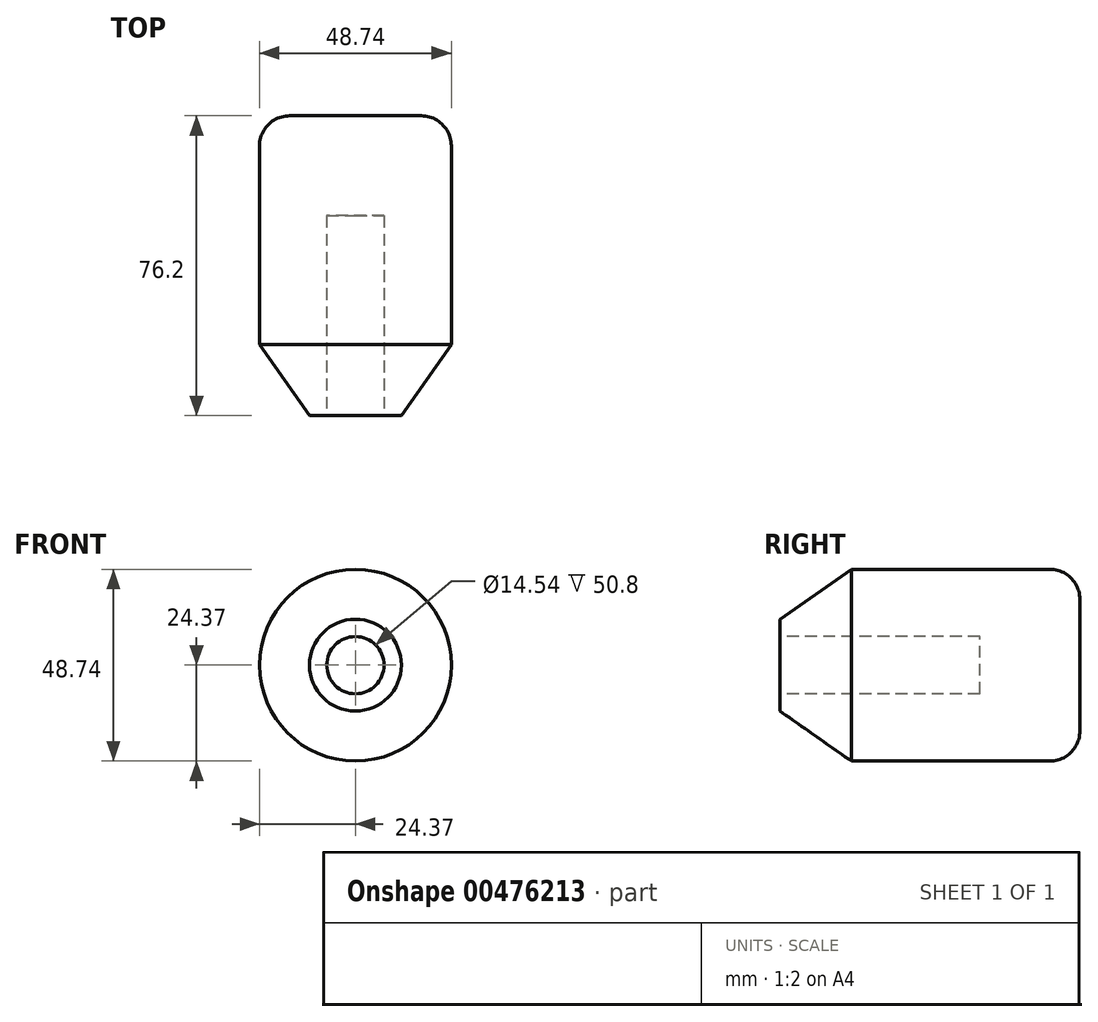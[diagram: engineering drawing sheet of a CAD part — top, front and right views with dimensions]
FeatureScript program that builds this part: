
annotation { "Feature Type Name" : "Feature", "Feature Type Description" : "" }
export const myFeature = defineFeature(function(context is Context, id is Id, definition is map)
    precondition{}
    {
        {
            var Q0;
            Q0=qCreatedBy(makeId("Front.planeOp"),FACE);
            var sketch = newSketch(context, id + "F0", { "sketchPlane" : qUnion([Q0])});
            skCircle(sketch, "E0", {"center": v(0, 0) * mm, "radius": 24.37 * mm});
            skSolve(sketch);
        }
        {
            var Q0;
            Q0 = qSketchRegion(id + "F0", true);
            extrude(context, id + "F1", {"entities" : qUnion([Q0]), "depth" : 76.2 * mm});
        }
        {
            var Q0;
            Q0=makeQuery(id+"F1.opExtrude","CAP_EDGE",EDGE,{"disambiguationData":[OSD([sQuery(id+"F0.wireOp",EDGE,"E0")])],"isStart":true});
            fillet(context, id + "F2", {"entities" : qUnion([Q0]), "radius" : 7.62 * mm, "tangentPropagation" : true, "allowEdgeOverflow" : false});
        }
        {
            var Q0;
            Q0=makeQuery(id+"F1.opExtrude","CAP_FACE",FACE,{"disambiguationData":[OSD([sQuery(id+"F0.wireOp",EDGE,"E0")])],"isStart":false});
            var sketch = newSketch(context, id + "F3", { "sketchPlane" : qUnion([Q0])});
            skCircle(sketch, "E1", {"center": v(0, 0) * mm, "radius": 7.27 * mm});
            skSolve(sketch);
        }
        {
            var Q0;
            Q0 = qSketchRegion(id + "F3", true);
            extrude(context, id + "F4", {"entities" : qUnion([Q0]), "operationType" : NewBodyOperationType.REMOVE, "oppositeDirection" : true, "depth" : 50.8 * mm});
        }
        {
            var Q0;
            Q0=makeQuery(id+"F1.opExtrude","CAP_EDGE",EDGE,{"disambiguationData":[OSD([sQuery(id+"F0.wireOp",EDGE,"E0")])],"isStart":false});
            chamfer(context, id + "F5", {"entities" : qUnion([Q0]), "chamferType" : ChamferType.OFFSET_ANGLE, "width" : 12.7 * mm, "oppositeDirection" : false, "angle" : 55 * degree, "tangentPropagation" : true});
        }
    });
